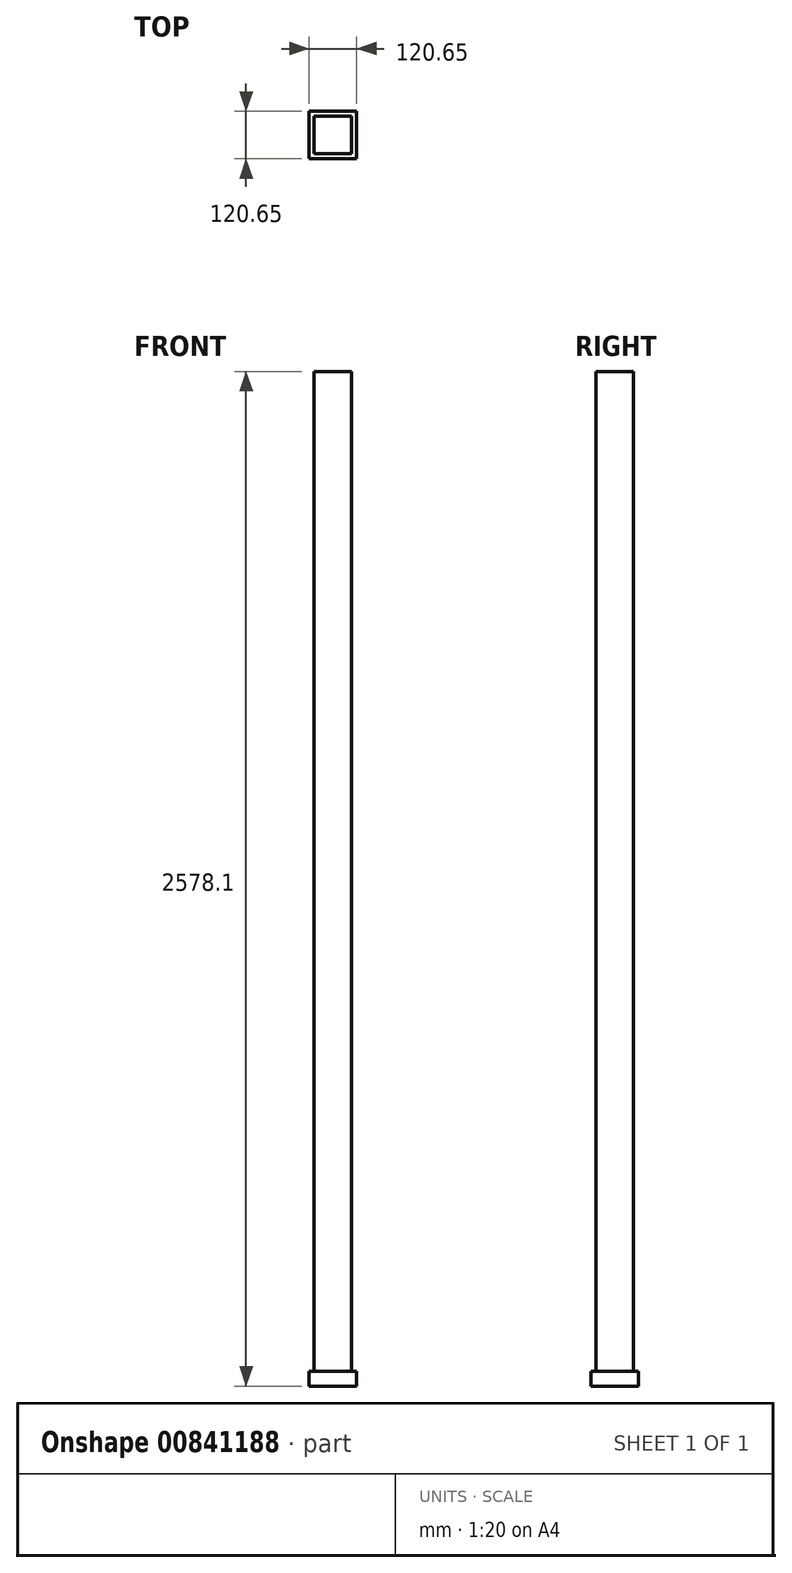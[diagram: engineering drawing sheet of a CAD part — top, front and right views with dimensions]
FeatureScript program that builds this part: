
annotation { "Feature Type Name" : "Feature", "Feature Type Description" : "" }
export const myFeature = defineFeature(function(context is Context, id is Id, definition is map)
    precondition{}
    {
        {
            var Q0;
            Q0=qCreatedBy(makeId("Top.planeOp"),FACE);
            var sketch = newSketch(context, id + "F0", { "sketchPlane" : qUnion([Q0])});
            skLineSegment(sketch, "E0.bottom", {"start": v(0, 0) * mm, "end": v(95.25, 0) * mm});
            skLineSegment(sketch, "E0.top", {"start": v(0, -95.25) * mm, "end": v(95.25, -95.25) * mm});
            skLineSegment(sketch, "E0.left", {"start": v(0, 0) * mm, "end": v(0, -95.25) * mm});
            skLineSegment(sketch, "E0.right", {"start": v(95.25, 0) * mm, "end": v(95.25, -95.25) * mm});
            skSolve(sketch);
        }
        {
            var Q0;
            Q0=makeQuery(id+"F0.imprint","IMPRINT",FACE,{"disambiguationData":[TD([[makeQuery(id+"F0.imprint","IMPRINT",EDGE,{"derivedFrom":sQuery(id+"F0.wireOp",EDGE,"E0.bottom")}),-1.0]])]});
            extrude(context, id + "F1", {"entities" : qUnion([Q0]), "depth" : 2540 * mm, "offsetDistance" : 25.4 * mm});
        }
        {
            var Q0;
            Q0=makeQuery(id+"F1.opExtrude","CAP_FACE",FACE,{"disambiguationData":[OSD([sQuery(id+"F0.wireOp",EDGE,"E0.bottom"),sQuery(id+"F0.wireOp",EDGE,"E0.top"),sQuery(id+"F0.wireOp",EDGE,"E0.left"),sQuery(id+"F0.wireOp",EDGE,"E0.right")])],"isStart":true});
            var sketch = newSketch(context, id + "F2", { "sketchPlane" : qUnion([Q0])});
            skLineSegment(sketch, "E1.bottom", {"start": v(-12.7, -12.7) * mm, "end": v(107.95, -12.7) * mm});
            skLineSegment(sketch, "E1.top", {"start": v(-12.7, 107.95) * mm, "end": v(107.95, 107.95) * mm});
            skLineSegment(sketch, "E1.left", {"start": v(-12.7, -12.7) * mm, "end": v(-12.7, 107.95) * mm});
            skLineSegment(sketch, "E1.right", {"start": v(107.95, -12.7) * mm, "end": v(107.95, 107.95) * mm});
            skSolve(sketch);
        }
        {
            var Q0;
            Q0=makeQuery(id+"F2.imprint","IMPRINT",FACE,{"disambiguationData":[TD([[makeQuery(id+"F2.imprint","IMPRINT",EDGE,{"derivedFrom":sQuery(id+"F2.wireOp",EDGE,"E1.bottom")}),1.0]])]});
            var Q1;
            Q1=makeQuery(id+"F2.imprint","IMPRINT",FACE,{"disambiguationData":[TD([[makeQuery(id+"F2.imprint","IMPRINT",EDGE,{"derivedFrom":makeQuery(id+"F1.opExtrude","CAP_EDGE",EDGE,{"disambiguationData":[OSD([sQuery(id+"F0.wireOp",EDGE,"E0.bottom")])],"isStart":true})}),1.0]])]});
            extrude(context, id + "F3", {"entities" : qUnion([Q0, Q1]), "operationType" : NewBodyOperationType.ADD, "depth" : 38.1 * mm, "offsetDistance" : 25.4 * mm});
        }
    });
